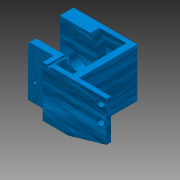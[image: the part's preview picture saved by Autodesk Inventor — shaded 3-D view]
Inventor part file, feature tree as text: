
AUTODESK INVENTOR PART (.ipt)
format: ipt  version: 2015 (Build 190159000, 159)  size: 163,328 bytes
history: native  units: in
note: dims shown in document units (in); Inventor stores cm internally (conversion verified against a paired STEP export)
features: sketch x10, other x3
ambient origin geometry x8: Origin, YZ Plane, XZ Plane, XY Plane, X Axis, Y Axis, Z Axis, Center Point
bodies: Solid1 (feature_tree)
feature tree (13):
  other  "Encoder Mount v2.ipt"
  other  "Solid1::Encoder Mount v2.ipt"
  other  "TaggingFeature1"
  sketch  "Sketch1"  dims[d0=0.3937in]
  sketch  "Sketch2"
  sketch  "Sketch3"
  sketch  "Sketch4"
  sketch  "Sketch5"
  sketch  "Sketch6"
  sketch  "Sketch7"
  sketch  "Sketch8"
  sketch  "Sketch9"
  sketch  "Sketch10"
